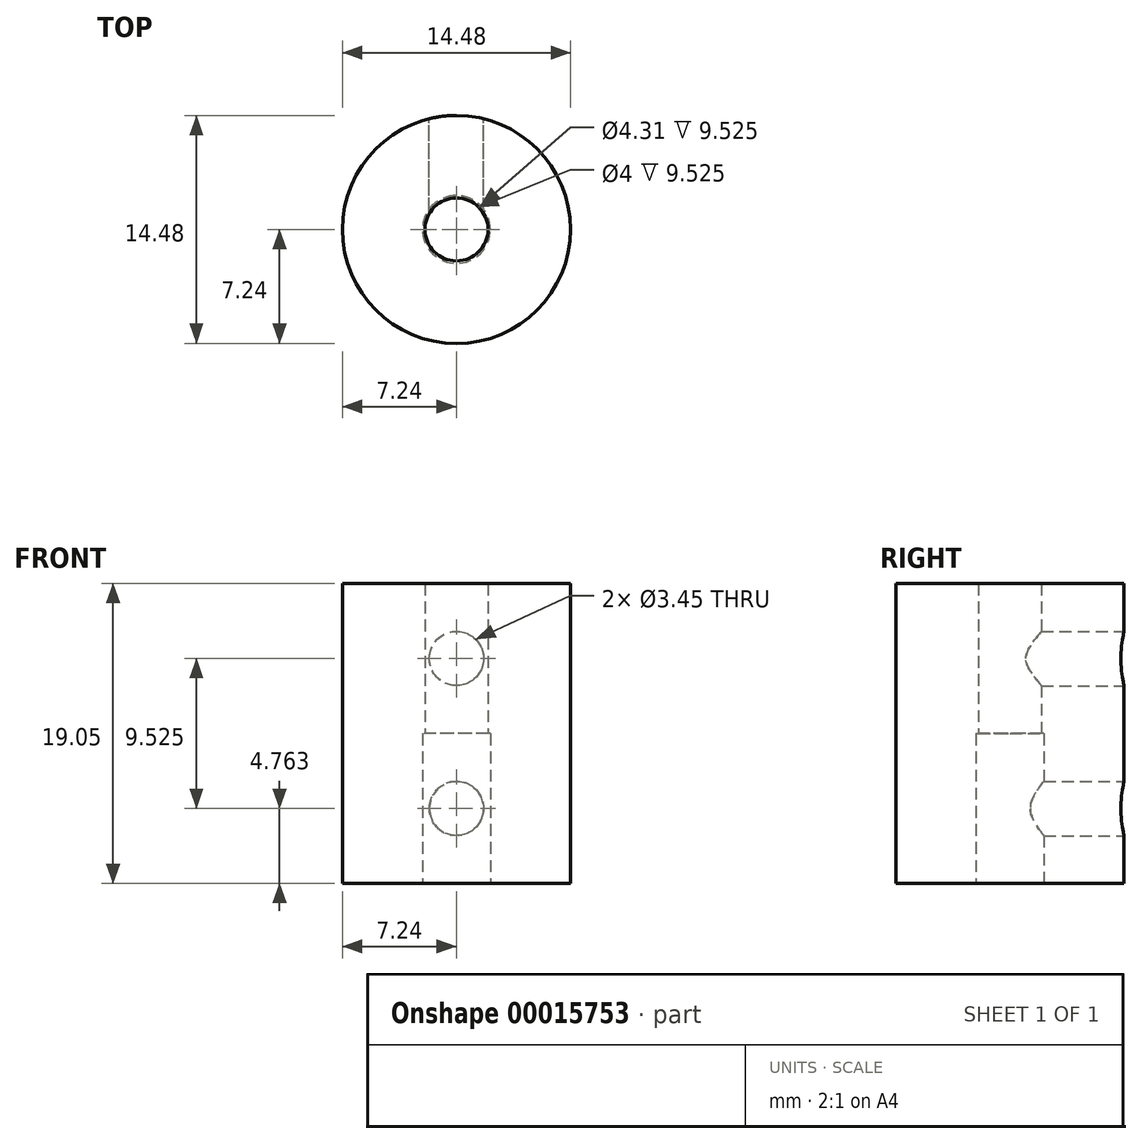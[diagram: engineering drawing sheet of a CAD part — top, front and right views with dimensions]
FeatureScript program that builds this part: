
annotation { "Feature Type Name" : "Feature", "Feature Type Description" : "" }
export const myFeature = defineFeature(function(context is Context, id is Id, definition is map)
    precondition{}
    {
        {
            var Q0;
            Q0=qCreatedBy(makeId("Top.planeOp"),FACE);
            var sketch = newSketch(context, id + "F0", { "sketchPlane" : qUnion([Q0])});
            skCircle(sketch, "E0", {"center": v(0, 0) * mm, "radius": 7.24 * mm, "construction": true});
            skCircle(sketch, "E1", {"center": v(0, 0) * mm, "radius": 2.15 * mm});
            skLineSegment(sketch, "E2.bottom", {"start": v(7.24, -7.24) * mm, "end": v(-7.24, -7.24) * mm});
            skLineSegment(sketch, "E2.top", {"start": v(7.24, 7.24) * mm, "end": v(-7.24, 7.24) * mm});
            skLineSegment(sketch, "E2.left", {"start": v(7.24, -7.24) * mm, "end": v(7.24, 7.24) * mm});
            skLineSegment(sketch, "E2.right", {"start": v(-7.24, -7.24) * mm, "end": v(-7.24, 7.24) * mm});
            skLineSegment(sketch, "E3.bottom", {"start": v(6.92, -2.15) * mm, "end": v(2.15, -2.15) * mm, "construction": true});
            skLineSegment(sketch, "E3.top", {"start": v(6.92, 2.15) * mm, "end": v(2.15, 2.15) * mm, "construction": true});
            skLineSegment(sketch, "E3.left", {"start": v(6.92, -2.15) * mm, "end": v(6.92, 2.15) * mm, "construction": true});
            skLineSegment(sketch, "E3.right", {"start": v(2.15, -2.15) * mm, "end": v(2.15, 2.15) * mm, "construction": true});
            skSolve(sketch);
        }
        {
            var Q0;
            Q0 = qSketchRegion(id + "F0", true);
            extrude(context, id + "F1", {"entities" : qUnion([Q0]), "depth" : 9.52 * mm});
        }
        {
            var Q0;
            Q0=makeQuery(id+"F1.opExtrude","CAP_FACE",FACE,{"disambiguationData":[OSD([sQuery(id+"F0.wireOp",EDGE,"E1"),sQuery(id+"F0.wireOp",EDGE,"E2.bottom"),sQuery(id+"F0.wireOp",EDGE,"E2.top"),sQuery(id+"F0.wireOp",EDGE,"E2.left"),sQuery(id+"F0.wireOp",EDGE,"E2.right")])],"isStart":false});
            var sketch = newSketch(context, id + "F2", { "sketchPlane" : qUnion([Q0])});
            skCircle(sketch, "E4", {"center": v(0, 0) * mm, "radius": 2 * mm});
            skLineSegment(sketch, "E5.bottom", {"start": v(7.24, 7.24) * mm, "end": v(-7.24, 7.24) * mm});
            skLineSegment(sketch, "E5.top", {"start": v(7.24, -7.24) * mm, "end": v(-7.24, -7.24) * mm});
            skLineSegment(sketch, "E5.left", {"start": v(7.24, 7.24) * mm, "end": v(7.24, -7.24) * mm});
            skLineSegment(sketch, "E5.right", {"start": v(-7.24, 7.24) * mm, "end": v(-7.24, -7.24) * mm});
            skSolve(sketch);
        }
        {
            var Q0;
            Q0 = qSketchRegion(id + "F2", true);
            extrude(context, id + "F3", {"entities" : qUnion([Q0]), "operationType" : NewBodyOperationType.ADD, "depth" : 9.52 * mm});
        }
        {
            var Q0;
            Q0=makeQuery(id+"F3.boolean.opBoolean","MERGE",FACE,{"derivedFrom":[makeQuery(id+"F1.opExtrude","SWEPT_FACE",FACE,{"disambiguationData":[OSD([sQuery(id+"F0.wireOp",EDGE,"E2.top")])]}),makeQuery(id+"F3.opExtrude","SWEPT_FACE",FACE,{"disambiguationData":[OSD([sQuery(id+"F2.wireOp",EDGE,"E5.bottom")])]})]});
            var sketch = newSketch(context, id + "F4", { "sketchPlane" : qUnion([Q0])});
            skLineSegment(sketch, "E6", {"start": v(0, 0) * mm, "end": v(0, 9.53) * mm, "construction": true});
            skLineSegment(sketch, "E7", {"start": v(0, 9.53) * mm, "end": v(0, 19.05) * mm, "construction": true});
            skCircle(sketch, "E8", {"center": v(0, 4.76) * mm, "radius": 1.73 * mm});
            skCircle(sketch, "E9", {"center": v(0, 14.29) * mm, "radius": 1.73 * mm});
            skSolve(sketch);
        }
        {
            var Q0;
            Q0 = qSketchRegion(id + "F4", true);
            var Q1;
            Q1=makeQuery(id+"F3.opExtrude","SWEPT_FACE",FACE,{"disambiguationData":[OSD([sQuery(id+"F2.wireOp",EDGE,"E4")])]});
            extrude(context, id + "F5", {"entities" : qUnion([Q0]), "operationType" : NewBodyOperationType.REMOVE, "endBound" : BoundingType.UP_TO_SURFACE, "oppositeDirection" : true, "endBoundEntityFace" : qUnion([Q1]), "depth" : 25.4 * mm});
        }
        {
            var Q0;
            Q0=makeQuery(id+"F3.boolean.opBoolean","MERGE",EDGE,{"derivedFrom":[makeQuery(id+"F1.opExtrude","SWEPT_EDGE",EDGE,{"disambiguationData":[OSD([sQuery(id+"F0.wireOp",EDGE,"E2.bottom"),sQuery(id+"F0.wireOp",EDGE,"E2.left")])]}),makeQuery(id+"F3.opExtrude","SWEPT_EDGE",EDGE,{"disambiguationData":[OSD([sQuery(id+"F2.wireOp",EDGE,"E5.top"),sQuery(id+"F2.wireOp",EDGE,"E5.left")])]})]});
            var Q1;
            Q1=makeQuery(id+"F3.boolean.opBoolean","MERGE",EDGE,{"derivedFrom":[makeQuery(id+"F1.opExtrude","SWEPT_EDGE",EDGE,{"disambiguationData":[OSD([sQuery(id+"F0.wireOp",EDGE,"E2.top"),sQuery(id+"F0.wireOp",EDGE,"E2.left")])]}),makeQuery(id+"F3.opExtrude","SWEPT_EDGE",EDGE,{"disambiguationData":[OSD([sQuery(id+"F2.wireOp",EDGE,"E5.bottom"),sQuery(id+"F2.wireOp",EDGE,"E5.left")])]})]});
            var Q2;
            Q2=makeQuery(id+"F3.boolean.opBoolean","MERGE",EDGE,{"derivedFrom":[makeQuery(id+"F1.opExtrude","SWEPT_EDGE",EDGE,{"disambiguationData":[OSD([sQuery(id+"F0.wireOp",EDGE,"E2.top"),sQuery(id+"F0.wireOp",EDGE,"E2.right")])]}),makeQuery(id+"F3.opExtrude","SWEPT_EDGE",EDGE,{"disambiguationData":[OSD([sQuery(id+"F2.wireOp",EDGE,"E5.bottom"),sQuery(id+"F2.wireOp",EDGE,"E5.right")])]})]});
            var Q3;
            Q3=makeQuery(id+"F3.boolean.opBoolean","MERGE",EDGE,{"derivedFrom":[makeQuery(id+"F1.opExtrude","SWEPT_EDGE",EDGE,{"disambiguationData":[OSD([sQuery(id+"F0.wireOp",EDGE,"E2.bottom"),sQuery(id+"F0.wireOp",EDGE,"E2.right")])]}),makeQuery(id+"F3.opExtrude","SWEPT_EDGE",EDGE,{"disambiguationData":[OSD([sQuery(id+"F2.wireOp",EDGE,"E5.top"),sQuery(id+"F2.wireOp",EDGE,"E5.right")])]})]});
            fillet(context, id + "F6", {"entities" : qUnion([Q0, Q1, Q2, Q3]), "radius" : 7.24 * mm, "tangentPropagation" : true, "allowEdgeOverflow" : false});
        }
    });
